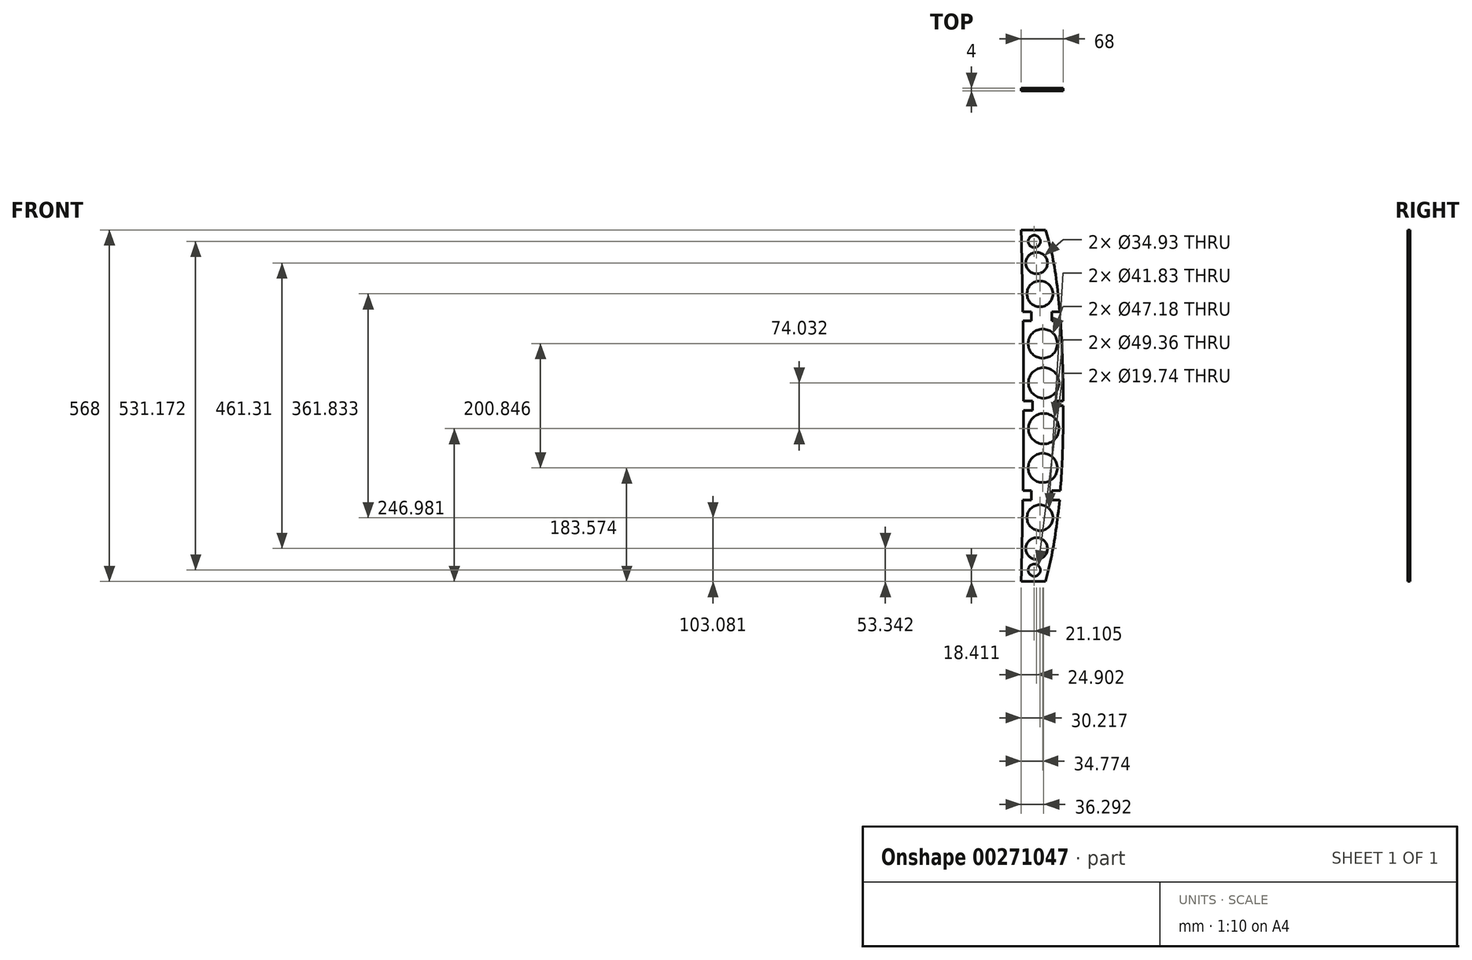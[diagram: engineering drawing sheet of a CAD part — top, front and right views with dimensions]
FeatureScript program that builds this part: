
annotation { "Feature Type Name" : "Feature", "Feature Type Description" : "" }
export const myFeature = defineFeature(function(context is Context, id is Id, definition is map)
    precondition{}
    {
        {
            var Q0;
            Q0=qCreatedBy(makeId("Front.planeOp"),FACE);
            var sketch = newSketch(context, id + "F0", { "sketchPlane" : qUnion([Q0])});
            skLineSegment(sketch, "E0", {"start": v(-144.64, 70.43) * mm, "end": v(-144.64, -213.57) * mm});
            skLineSegment(sketch, "E1", {"start": v(-144.64, -213.57) * mm, "end": v(-105.64, -213.57) * mm});
            skLineSegment(sketch, "E2.MirrorCS", {"start": v(-144.64, 70.43) * mm, "end": v(-144.64, 354.43) * mm});
            skLineSegment(sketch, "E3.MirrorCS", {"start": v(-144.64, 354.43) * mm, "end": v(-105.64, 354.43) * mm});
            skFitSpline(sketch, "E4", {"points": [v(-105.64, 354.43) * mm, v(-76.64, 70.43) * mm, v(-105.64, -213.57) * mm], "startDerivative": vector(127.3, -340.95) * mm, "endDerivative": vector(-129.68, -456.94) * mm});
            skLineSegment(sketch, "E5", {"start": v(-144.64, 70.43) * mm, "end": v(-140.64, 70.43) * mm});
            skFitSpline(sketch, "E6", {"points": [v(-144.64, 354.43) * mm, v(-140.64, 70.43) * mm, v(-144.64, -213.57) * mm], "startDerivative": vector(12, -568) * mm, "endDerivative": vector(-12, -568) * mm});
            skLineSegment(sketch, "E7", {"start": v(-126.65, 70.43) * mm, "end": v(-126.65, 77.93) * mm});
            skLineSegment(sketch, "E8", {"start": v(-126.65, 77.93) * mm, "end": v(-140.65, 77.93) * mm});
            skLineSegment(sketch, "E9", {"start": v(-90.66, 77.93) * mm, "end": v(-90.66, 70.43) * mm});
            skLineSegment(sketch, "E10", {"start": v(-90.66, 77.93) * mm, "end": v(-76.66, 77.93) * mm});
            skLineSegment(sketch, "E11.MirrorCS", {"start": v(-90.67, 62.93) * mm, "end": v(-76.67, 62.93) * mm});
            skLineSegment(sketch, "E12.MirrorCS", {"start": v(-126.65, 62.93) * mm, "end": v(-140.65, 62.93) * mm});
            skLineSegment(sketch, "E13.MirrorCS", {"start": v(-126.65, 70.43) * mm, "end": v(-126.65, 62.93) * mm});
            skLineSegment(sketch, "E14.MirrorCS", {"start": v(-90.67, 62.93) * mm, "end": v(-90.67, 70.43) * mm});
            skLineSegment(sketch, "E15", {"start": v(-76.64, 70.43) * mm, "end": v(-144.64, 70.43) * mm});
            skLineSegment(sketch, "E16", {"start": v(-140.65, 77.93) * mm, "end": v(-140.65, 77.93) * mm});
            skLineSegment(sketch, "E17", {"start": v(-140.64, 70.43) * mm, "end": v(-141.2, 70.43) * mm});
            skLineSegment(sketch, "E18", {"start": v(-140.65, 77.93) * mm, "end": v(-141.52, 77.93) * mm});
            skLineSegment(sketch, "E19", {"start": v(-41.55, 214.93) * mm, "end": v(-174.23, 214.93) * mm});
            skLineSegment(sketch, "E20", {"start": v(-95.23, 214.93) * mm, "end": v(-95.23, 222.43) * mm});
            skLineSegment(sketch, "E21", {"start": v(-95.23, 214.93) * mm, "end": v(-95.23, 207.43) * mm});
            skLineSegment(sketch, "E22", {"start": v(-95.23, 207.43) * mm, "end": v(-81.23, 207.43) * mm});
            skLineSegment(sketch, "E23", {"start": v(-95.23, 222.43) * mm, "end": v(-82.4, 222.43) * mm});
            skLineSegment(sketch, "E24", {"start": v(-128.05, 214.93) * mm, "end": v(-128.05, 222.43) * mm});
            skLineSegment(sketch, "E25", {"start": v(-128.05, 222.43) * mm, "end": v(-142.05, 222.43) * mm});
            skLineSegment(sketch, "E26", {"start": v(-128.05, 214.93) * mm, "end": v(-128.05, 207.43) * mm});
            skLineSegment(sketch, "E27", {"start": v(-128.05, 207.43) * mm, "end": v(-142.05, 207.43) * mm});
            skCircle(sketch, "E28", {"center": v(-108.35, 107.44) * mm, "radius": 24.68 * mm});
            skCircle(sketch, "E29", {"center": v(-109.87, 170.85) * mm, "radius": 23.59 * mm});
            skCircle(sketch, "E30", {"center": v(-114.42, 251.34) * mm, "radius": 20.91 * mm});
            skCircle(sketch, "E31", {"center": v(-119.74, 301.08) * mm, "radius": 17.47 * mm});
            skCircle(sketch, "E32", {"center": v(-123.54, 336.01) * mm, "radius": 9.87 * mm});
            skCircle(sketch, "E33.MirrorC", {"center": v(-108.35, 33.41) * mm, "radius": 24.68 * mm});
            skCircle(sketch, "E34.MirrorC", {"center": v(-109.87, -30) * mm, "radius": 23.59 * mm});
            skLineSegment(sketch, "E35.MirrorCS", {"start": v(-95.23, -74.07) * mm, "end": v(-95.23, -81.57) * mm});
            skLineSegment(sketch, "E36.MirrorCS", {"start": v(-128.05, -66.57) * mm, "end": v(-142.05, -66.57) * mm});
            skLineSegment(sketch, "E37.MirrorCS", {"start": v(-95.23, -66.57) * mm, "end": v(-81.23, -66.57) * mm});
            skLineSegment(sketch, "E38.MirrorCS", {"start": v(-128.05, -74.07) * mm, "end": v(-128.05, -66.57) * mm});
            skLineSegment(sketch, "E39.MirrorCS", {"start": v(-95.23, -81.57) * mm, "end": v(-82.4, -81.57) * mm});
            skLineSegment(sketch, "E40.MirrorCS", {"start": v(-128.05, -74.07) * mm, "end": v(-128.05, -81.57) * mm});
            skLineSegment(sketch, "E41.MirrorCS", {"start": v(-95.23, -74.07) * mm, "end": v(-95.23, -66.57) * mm});
            skLineSegment(sketch, "E42.MirrorCS", {"start": v(-128.05, -81.57) * mm, "end": v(-142.05, -81.57) * mm});
            skCircle(sketch, "E43.MirrorC", {"center": v(-114.42, -110.49) * mm, "radius": 20.91 * mm});
            skCircle(sketch, "E44.MirrorC", {"center": v(-119.74, -160.23) * mm, "radius": 17.47 * mm});
            skCircle(sketch, "E45.MirrorC", {"center": v(-123.54, -195.16) * mm, "radius": 9.87 * mm});
            skSolve(sketch);
        }
        {
            var Q0;
            {var subQ4=sQuery(id+"F0.wireOp",EDGE,"E3.MirrorCS");Q0=makeQuery(id+"F0.imprint","IMPRINT",FACE,{"disambiguationData":[TD([[makeQuery(id+"F0.imprint","IMPRINT",EDGE,{"derivedFrom":subQ4}),-1.0]])]});}
            var Q1;
            {var subQ1=sQuery(id+"F0.wireOp",EDGE,"E7");Q1=makeQuery(id+"F0.imprint","IMPRINT",FACE,{"disambiguationData":[TD([[makeQuery(id+"F0.imprint","IMPRINT",EDGE,{"derivedFrom":subQ1}),-1.0]])]});}
            var Q2;
            {var subQ13=sQuery(id+"F0.wireOp",EDGE,"E1");Q2=makeQuery(id+"F0.imprint","IMPRINT",FACE,{"disambiguationData":[TD([[makeQuery(id+"F0.imprint","IMPRINT",EDGE,{"derivedFrom":subQ13}),1.0]])]});}
            extrude(context, id + "F1", {"entities" : qUnion([Q0, Q1, Q2]), "depth" : 4 * mm});
        }
    });
